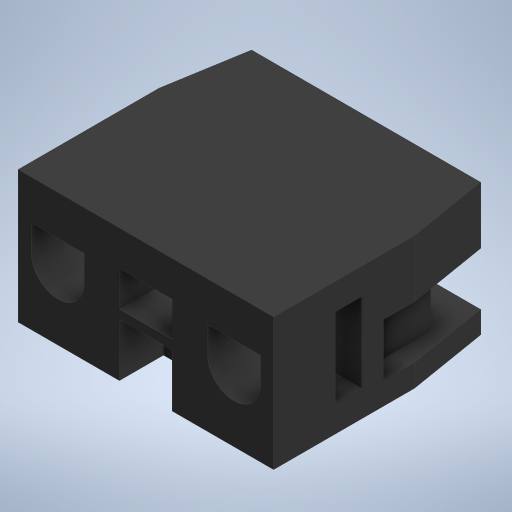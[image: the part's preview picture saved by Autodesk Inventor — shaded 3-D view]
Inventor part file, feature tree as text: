
AUTODESK INVENTOR PART (.ipt)
format: ipt  version: 2023 (Build 270158000, 158)  size: 399,872 bytes
history: native  units: mm
features: sketch x12, extrude x10, other x3, hole x2
ambient origin geometry x8: Origin, YZ Plane, XZ Plane, XY Plane, X Axis, Y Axis, Z Axis, Center Point
bodies: Body1 (feature_tree)
feature tree (27):
  other  "Sólido1"
  extrude  "Extrusão1"  Depth=15.0mm
  extrude  "Extrusão2"  Depth=9.0mm
  extrude  "Extrusão3"  Depth=26.0mm
  extrude  "Extrusão4"  Depth=6.0mm
  extrude  "Extrusão5"  Depth=10.0mm
  extrude  "Extrusão6"  Depth=6.0mm
  hole  "Furo1"  [1 undecoded]
  extrude  "Extrusão7"  Depth=3.0mm
  extrude  "Extrusão8"  TaperAngle=0.0deg  [1 undecoded]
  extrude  "Extrusão9"  Depth=3.0mm
  hole  "Furo2"  [1 undecoded]
  extrude  "Extrusão11"  Depth=6.0mm
  sketch  "Esboço1"  dims[d0=29.0mm d1=15.0mm]
  sketch  "Esboço2"  dims[d2=25.0mm d3=0.0mm d4=9.0mm]
  other  "Contorno projetado1"
  sketch  "Esboço3"  dims[d5=9.0mm d6=26.0mm]
  sketch  "Esboço4"  dims[d7=0.0mm d8=0.0mm d9=6.0mm]
  sketch  "Esboço5"  dims[d10=6.0mm d11=10.0mm]
  sketch  "Esboço6"  dims[d12=10.0mm d13=6.0mm]
  sketch  "Esboço8"  dims[d14=6.0mm d15=0.0mm]
  sketch  "Esboço9"  dims[d16=10.0mm d17=0.0mm d18=3.0mm]
  sketch  "Esboço10"  dims[d19=9.0mm d20=0.0mm]
  sketch  "Esboço11"  dims[d21=7.5mm d22=0.0mm d23=3.0mm]
  sketch  "Esboço12"  dims[d24=9.0mm d25=0.0mm]
  sketch  "Esboço14"  dims[d26=7.5mm d27=0.0mm d28=6.0mm d29=6.0mm d30=0.0mm d31=6.0mm d32=4.0mm d33=5.0mm d34=0.0mm d35=3.0mm d36=4.0mm d37=4.0mm d38=2.0mm d39=90.0deg d40=4.0mm d41=20.594885mm d42=2.0mm d43=0.0mm d44=5.0mm d45=1.0mm d46=0.0mm d47=7.0mm d48=6.0mm d49=0.0mm d50=2.5mm d51=7.0mm d52=6.0mm d53=0.0mm d54=2.5mm d55=5.0mm d56=0.0mm d57=3.0mm d58=6.0mm d59=3.0mm d60=6.0mm d61=7.5mm d62=0.0mm d63=3.0mm d64=0.599mm d65=4.0mm d66=2.0mm d67=90.0deg d68=0.998mm d69=20.594885mm d70=0.0mm d71=0.0mm d72=0.0mm d73=0.0mm d80=0.0mm d81=0.0mm]
  other  "Contorno projetado2"
note: 3 required parameter values undecoded (feature->parameter linkage not recoverable at this tier; creation-order binding heuristic only, values carry confidence <= 0.55)
